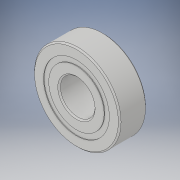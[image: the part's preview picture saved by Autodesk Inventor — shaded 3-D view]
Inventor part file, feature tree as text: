
AUTODESK INVENTOR PART (.ipt)
format: ipt  version: 2018 (Build 220112000, 112)  size: 458,752 bytes
history: native  units: in
note: dims shown in document units (in); Inventor stores cm internally (conversion verified against a paired STEP export)
features: other x7, revolve x5
ambient origin geometry x8: Origin, YZ Plane, XZ Plane, XY Plane, X Axis, Y Axis, Z Axis, Center Point
bodies: Solid1 (feature_tree), Solid2 (feature_tree), Solid3 (feature_tree), Solid4 (feature_tree), Solid5 (feature_tree), Solid6 (feature_tree), Solid7 (feature_tree), Solid8 (feature_tree), Solid9 (feature_tree), Solid10 (feature_tree), Solid11 (feature_tree), Solid12 (feature_tree)
feature tree (12):
  revolve  "Revolve1"  [1 undecoded]
  revolve  "Revolve3"  [1 undecoded]
  revolve  "Revolve4"  [1 undecoded]
  other  "CirPattern1[1]"
  other  "CirPattern1[2]"
  other  "CirPattern1[3]"
  other  "CirPattern1[4]"
  other  "CirPattern1[5]"
  other  "CirPattern1[6]"
  other  "CirPattern1[7]"
  revolve  "Revolve5[1]"  [1 undecoded]
  revolve  "Revolve5[2]"  [1 undecoded]
note: 5 required parameter values undecoded (feature->parameter linkage not recoverable at this tier; creation-order binding heuristic only, values carry confidence <= 0.55)
